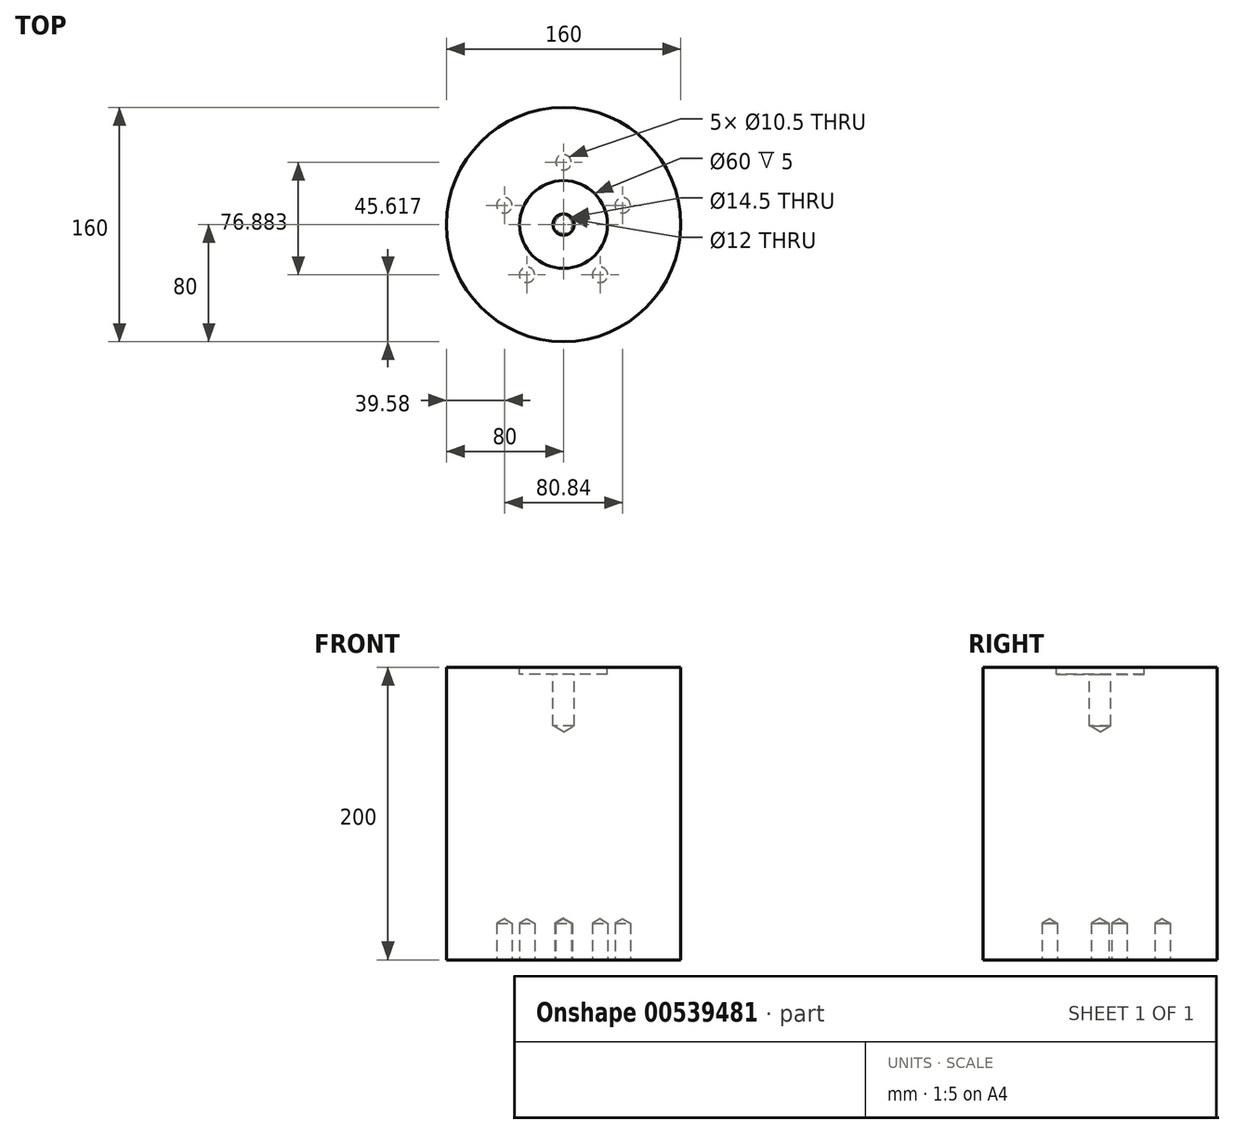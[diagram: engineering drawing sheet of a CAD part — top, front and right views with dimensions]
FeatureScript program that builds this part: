
annotation { "Feature Type Name" : "Feature", "Feature Type Description" : "" }
export const myFeature = defineFeature(function(context is Context, id is Id, definition is map)
    precondition{}
    {
        {
            var Q0;
            Q0=qCreatedBy(makeId("Top.planeOp"),FACE);
            var sketch = newSketch(context, id + "F0", { "sketchPlane" : qUnion([Q0])});
            skCircle(sketch, "E0", {"center": v(0, 0) * mm, "radius": 80 * mm});
            skSolve(sketch);
        }
        {
            var Q0;
            Q0=makeQuery(id+"F0.imprint","IMPRINT",FACE,{"disambiguationData":[TD([[makeQuery(id+"F0.imprint","IMPRINT",EDGE,{"derivedFrom":sQuery(id+"F0.wireOp",EDGE,"E0")}),1.0]])]});
            extrude(context, id + "F1", {"entities" : qUnion([Q0]), "depth" : 200 * mm, "offsetDistance" : 25 * mm});
        }
        {
            var Q0;
            Q0=makeQuery(id+"F1.opExtrude","CAP_FACE",FACE,{"disambiguationData":[OSD([sQuery(id+"F0.wireOp",EDGE,"E0")])],"isStart":false});
            var sketch = newSketch(context, id + "F2", { "sketchPlane" : qUnion([Q0])});
            skPoint(sketch, "E1", {"position": v(0, 0) * mm});
            skCircle(sketch, "E2", {"center": v(0, 0) * mm, "radius": 20 * mm});
            skPoint(sketch, "E3", {"position": v(0, 20) * mm});
            skPoint(sketch, "E4.1.0", {"position": v(-19.02, 6.18) * mm});
            skPoint(sketch, "E4.2.0", {"position": v(-11.76, -16.18) * mm});
            skPoint(sketch, "E4.3.0", {"position": v(11.76, -16.18) * mm});
            skPoint(sketch, "E4.4.0", {"position": v(19.02, 6.18) * mm});
            skCircle(sketch, "E5", {"center": v(0, 0) * mm, "radius": 30 * mm});
            skCircle(sketch, "E6", {"center": v(0, 0) * mm, "radius": 80 * mm});
            skSolve(sketch);
        }
        {
            var Q0;
            Q0=sQuery(id+"F2.wireOp",VERTEX,"E1");
            var Q1;
            Q1=makeQuery(id+"F1.opExtrude","SWEPT_BODY",BODY,{"disambiguationData":[OSD([sQuery(id+"F0.wireOp",EDGE,"E0")])]});
            hole(context, id + "F3", {"style" : HoleStyle.SIMPLE, "endStyle" : HoleEndStyle.BLIND, "standardTappedOrClearance" : lookupTablePath({ "standard" : "ISO", "engagement" : "75%", "pitch" : "1.5 mm", "size" : "M16", "type" : "Tapped" }), "standardBlindInLast" : lookupTablePath({ "standard" : "ISO", "engagement" : "75%", "pitch" : "1.5 mm", "size" : "M16", "type" : "Tapped" }), "holeDiameter" : 14.5 * mm, "showTappedDepth" : true, "holeDepth" : 40 * mm, "tappedDepth" : 35.5 * mm, "tapClearance" : 3, "locations" : qUnion([Q0]), "scope" : qUnion([Q1]), "majorDiameter" : 16 * mm});
        }
        {
            var Q0;
            Q0=makeQuery(id+"F2.imprint","IMPRINT",FACE,{"disambiguationData":[TD([[makeQuery(id+"F2.imprint","IMPRINT",EDGE,{"derivedFrom":sQuery(id+"F2.wireOp",EDGE,"E2")}),-1.0]])]});
            var Q1;
            Q1=makeQuery(id+"F2.imprint","IMPRINT",FACE,{"disambiguationData":[TD([[makeQuery(id+"F2.imprint","IMPRINT",EDGE,{"derivedFrom":sQuery(id+"F2.wireOp",EDGE,"E2")}),1.0]])]});
            extrude(context, id + "F4", {"entities" : qUnion([Q0, Q1]), "operationType" : NewBodyOperationType.REMOVE, "oppositeDirection" : true, "depth" : 5 * mm, "offsetDistance" : 25 * mm});
        }
        {
            var Q0;
            Q0=makeQuery(id+"F1.opExtrude","CAP_FACE",FACE,{"disambiguationData":[OSD([sQuery(id+"F0.wireOp",EDGE,"E0")])],"isStart":true});
            var sketch = newSketch(context, id + "F5", { "sketchPlane" : qUnion([Q0])});
            skCircle(sketch, "E7", {"center": v(0, 0) * mm, "radius": 42.5 * mm});
            skPoint(sketch, "E8", {"position": v(0, -42.5) * mm});
            skPoint(sketch, "E9.1.0", {"position": v(40.42, -13.13) * mm});
            skPoint(sketch, "E9.2.0", {"position": v(24.98, 34.38) * mm});
            skPoint(sketch, "E9.3.0", {"position": v(-24.98, 34.38) * mm});
            skPoint(sketch, "E9.4.0", {"position": v(-40.42, -13.13) * mm});
            skSolve(sketch);
        }
        {
            var Q0;
            Q0=sQuery(id+"F5.wireOp",VERTEX,"E9.3.0");
            var Q1;
            Q1=sQuery(id+"F5.wireOp",VERTEX,"E9.4.0");
            var Q2;
            Q2=sQuery(id+"F5.wireOp",VERTEX,"E8");
            var Q3;
            Q3=sQuery(id+"F5.wireOp",VERTEX,"E9.1.0");
            var Q4;
            Q4=sQuery(id+"F5.wireOp",VERTEX,"E9.2.0");
            var Q5;
            Q5=makeQuery(id+"F1.opExtrude","SWEPT_BODY",BODY,{"disambiguationData":[OSD([sQuery(id+"F0.wireOp",EDGE,"E0")])]});
            hole(context, id + "F6", {"style" : HoleStyle.SIMPLE, "endStyle" : HoleEndStyle.BLIND, "standardTappedOrClearance" : lookupTablePath({ "standard" : "ISO", "engagement" : "75%", "pitch" : "1.5 mm", "size" : "M12", "type" : "Tapped" }), "standardBlindInLast" : lookupTablePath({ "standard" : "ISO", "engagement" : "75%", "pitch" : "1.5 mm", "size" : "M12", "type" : "Tapped" }), "holeDiameter" : 10.5 * mm, "majorDiameter" : 12 * mm, "showTappedDepth" : true, "holeDepth" : 25 * mm, "tappedDepth" : 20.5 * mm, "tapClearance" : 3, "locations" : qUnion([Q0, Q1, Q2, Q3, Q4]), "scope" : qUnion([Q5])});
        }
        {
            var Q0;
            Q0=sQuery(id+"F0.wireOp",VERTEX,"E0.center");
            var Q1;
            Q1=makeQuery(id+"F1.opExtrude","SWEPT_BODY",BODY,{"disambiguationData":[OSD([sQuery(id+"F0.wireOp",EDGE,"E0")])]});
            hole(context, id + "F7", {"style" : HoleStyle.SIMPLE, "endStyle" : HoleEndStyle.BLIND, "oppositeDirection" : true, "standardTappedOrClearance" : lookupTablePath({ "standard" : "ISO", "size" : "12", "type" : "Drilled" }), "standardBlindInLast" : lookupTablePath({ "standard" : "ISO", "size" : "12", "type" : "Drilled" }), "holeDiameter" : 12 * mm, "majorDiameter" : 5 * mm, "holeDepth" : 25 * mm, "tappedDepth" : 20 * mm, "tapClearance" : 3, "locations" : qUnion([Q0]), "scope" : qUnion([Q1])});
        }
    });
